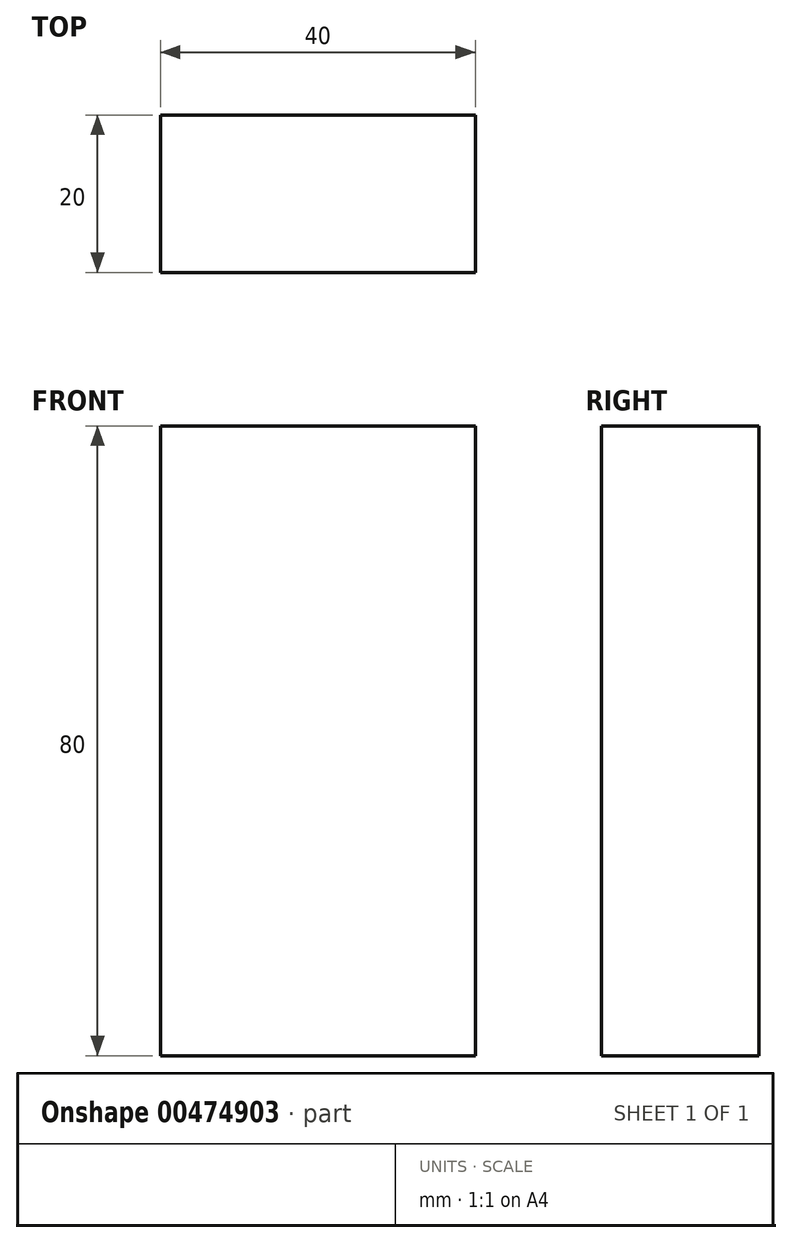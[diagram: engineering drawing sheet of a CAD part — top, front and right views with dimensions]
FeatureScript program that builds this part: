
annotation { "Feature Type Name" : "Feature", "Feature Type Description" : "" }
export const myFeature = defineFeature(function(context is Context, id is Id, definition is map)
    precondition{}
    {
        {
            var Q0;
            Q0=qCreatedBy(makeId("Front.planeOp"),FACE);
            var sketch = newSketch(context, id + "F0", { "sketchPlane" : qUnion([Q0])});
            skLineSegment(sketch, "E0.bottom", {"start": v(21, 40) * mm, "end": v(-19, 40) * mm});
            skLineSegment(sketch, "E0.top", {"start": v(21, -40) * mm, "end": v(-19, -40) * mm});
            skLineSegment(sketch, "E0.left", {"start": v(21, 40) * mm, "end": v(21, -40) * mm});
            skLineSegment(sketch, "E0.right", {"start": v(-19, 40) * mm, "end": v(-19, -40) * mm});
            skPoint(sketch, "E0.middle", {"position": v(1, 0) * mm});
            skSolve(sketch);
        }
        {
            var Q0;
            Q0 = qSketchRegion(id + "F0", true);
            extrude(context, id + "F1", {"entities" : qUnion([Q0]), "depth" : 20 * mm});
        }
    });
